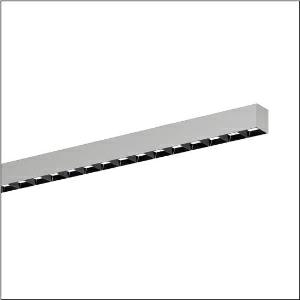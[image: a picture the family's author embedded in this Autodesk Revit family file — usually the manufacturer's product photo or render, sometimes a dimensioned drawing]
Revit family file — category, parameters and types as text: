
# Revit family: silica_r__21_51mx22dc4asb_d7c9
name_source: partatom
category: Lighting Fixtures
units: mm (PartAtom-declared; Revit-internal decimal feet)

## family parameters
Cut with Voids When Loaded = No
Host = Face
Light Source = No
Part Type = Normal
Room Calculation Point = No
Round Connector Dimension = Use Diameter
Shared = No

## types (1)
- --- (1 x LED, 10800 lm, 64.7 W, 4000K)
    Apparent Load = 65 VA
    CIE Flux Codes = 86 100 100 100 100
    Color Rendering = 80
    Color Temperature = 4000K
    Default Elevation = 1800 mm
    Description = Silica® 21, office luminaire, primary light control with darklight reflector, of PMMA, black, CAT 2 (L<= 3000cd/m²), light emission: direct distribution, primary light characteristic: symmetric, installation type: surface-mounted, LED, rated luminous flux: 10.800lm, luminous efficacy: 167lm/W, light colour: 840, colour temperature: 4000K, with terminal, 3+2-pole, max. 2.5mm², mains connection: 220..240V, AC, 50/60Hz, rated input power: 64.7W, luminaire housing, of aluminium, metallic grey (RAL 9006), length: 3.004mm, width: 53mm, height: 53mm, protection rating (complete): IP20, insulation class (complete): insulation class I (protective earthing), certification: CE, permissible operating ambient temperature: 0..+35°C, standard: EN 50419, packaging unit: 1 piece
    Height = 0 mm  [stored 0 ft]
    Lamp = 1 x LED
    Lamp Light Flux = 10800 lm
    Lamp Power = 64.7 W
    Lamp count = 1
    Length = 3004 mm
    Luminous efficacy = 167 lm/W
    Manufacturer = Siteco
    ModVariant = No
    Model = 51MX22DC4ASB
    Mounting Place = Ceiling
    Mounting Type = Recessed
    Number of Poles = 1
    OnlyDefault = Yes
    Power Factor = 1
    Product Name = Silica® 21
    Product group = office luminaire | ceiling recessed
    ProductGroupID = 401
    Protection Class = Protection class I
    Protection Degree = IP 20
    RLX_Detail_Level = 1
    RLX_Emergency_Light_Flux = 0 lm
    RLX_Emergency_Type = 0
    RLX_Emergency_Type_DB = No
    RlxData = <blob elided: 65197 chars, md5=082b5cb7>
    Socket = socket
    Standby Power = 0 W
    System Light Flux = 10800 lm
    System Power = 65 W
    Type Comments = factory setting: luminous flux: 100 % | dim-lin: 254 | 366 mA
    Type Image = l_1297764.jpg
    URL = http://relux.com
    VarID = @adj_055829
    Voltage = 0 V
    Weight = 0.00 kg
    Width = 53 mm

note: [stored X ft] marks values corroborated as IEEE doubles in the binary element streams (Revit-internal decimal feet)

## geometry (parser evidence)
native form markers: Blend x4, Sweep x10
no freeform markers — native parametric forms only
